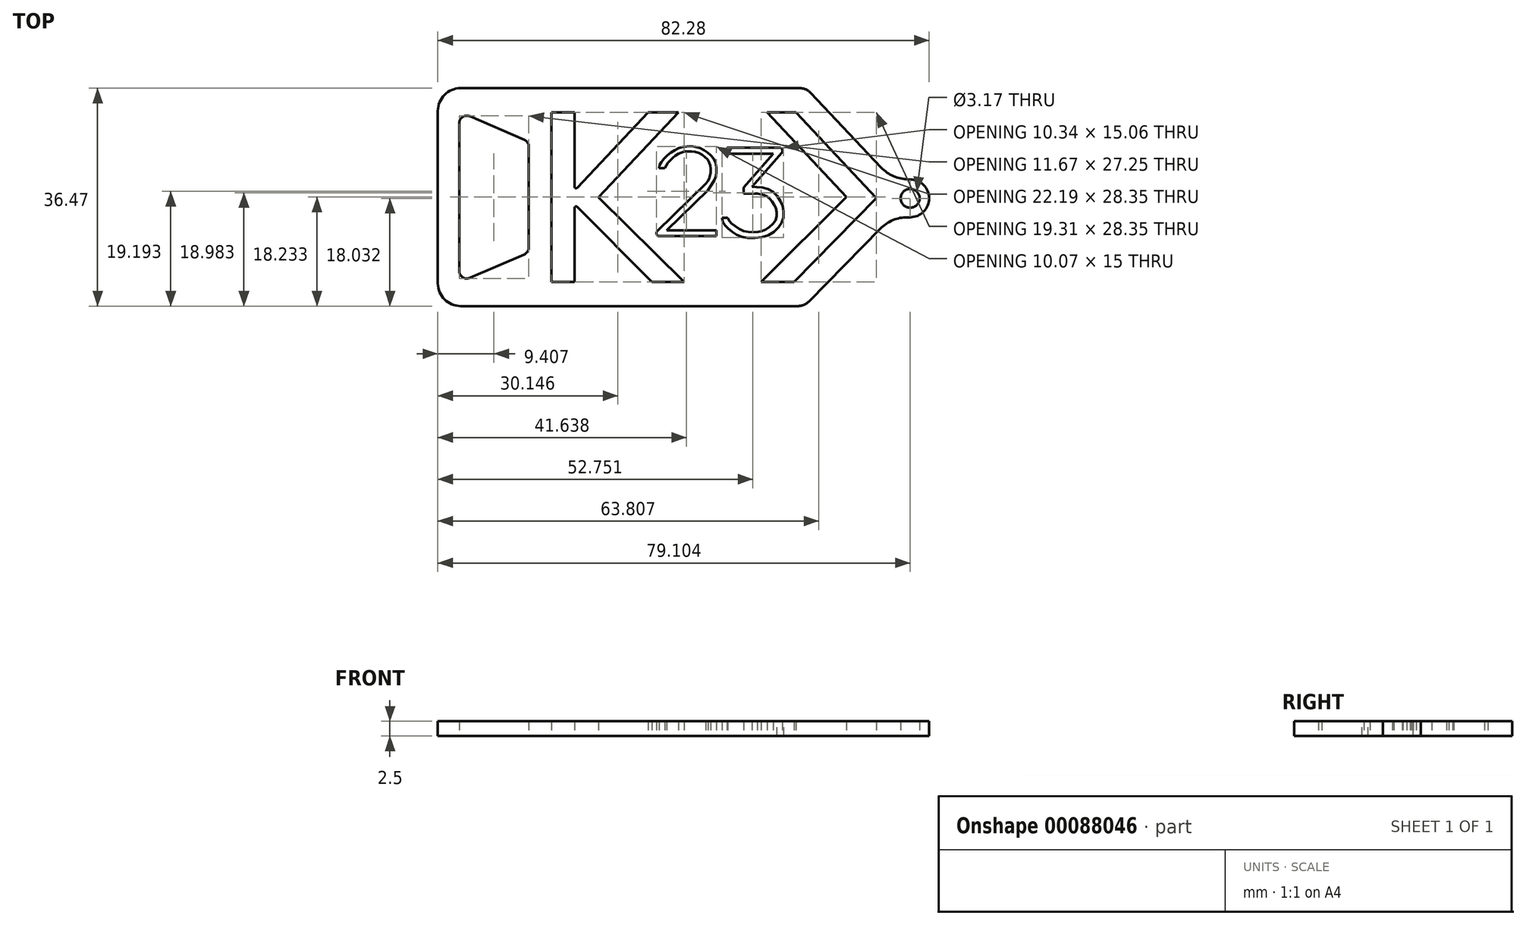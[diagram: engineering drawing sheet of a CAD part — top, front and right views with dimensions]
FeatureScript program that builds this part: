
annotation { "Feature Type Name" : "Feature", "Feature Type Description" : "" }
export const myFeature = defineFeature(function(context is Context, id is Id, definition is map)
    precondition{}
    {
        {
            var Q0;
            Q0=qCreatedBy(makeId("Top.planeOp"),FACE);
            var sketch = newSketch(context, id + "F0", { "sketchPlane" : qUnion([Q0])});
            skLineSegment(sketch, "E0", {"start": v(-56.05, -53.7) * mm, "end": v(-56.05, -52.7) * mm});
            skLineSegment(sketch, "E1", {"start": v(-56.05, -53.7) * mm, "end": v(-65.6, -53.7) * mm});
            skLineSegment(sketch, "E2", {"start": v(-65.96, -52.83) * mm, "end": v(-57.87, -44.95) * mm});
            skLineSegment(sketch, "E3", {"start": v(-56.05, -52.7) * mm, "end": v(-64.4, -52.7) * mm});
            skLineSegment(sketch, "E4", {"start": v(-64.4, -52.7) * mm, "end": v(-65.1, -52) * mm, "construction": true});
            skLineSegment(sketch, "E5", {"start": v(-64.4, -52.7) * mm, "end": v(-57.5, -45.98) * mm});
            skFitSpline(sketch, "E6", {"points": [v(-57.87, -44.95) * mm, v(-57.32, -44.18) * mm, v(-57.07, -43.34) * mm, v(-57.04, -42.12) * mm, v(-57.36, -41.17) * mm, v(-58.14, -40.3) * mm, v(-59.25, -39.7) * mm, v(-60.57, -39.5) * mm, v(-61.66, -39.6) * mm, v(-62.56, -40) * mm, v(-63.57, -40.77) * mm, v(-64.27, -41.53) * mm, v(-64.68, -42.35) * mm], "startDerivative": vector(10.41, 10.64) * mm, "endDerivative": vector(-4.73, -10.96) * mm});
            skLineSegment(sketch, "E7", {"start": v(-64.68, -42.35) * mm, "end": v(-65.68, -42.35) * mm});
            skFitSpline(sketch, "E8", {"points": [v(-65.68, -42.35) * mm, v(-65.54, -41.73) * mm, v(-65.05, -41) * mm, v(-64.16, -40.06) * mm, v(-63.3, -39.44) * mm, v(-62.23, -38.9) * mm, v(-61.22, -38.7) * mm, v(-60.27, -38.67) * mm, v(-59.04, -38.87) * mm, v(-57.9, -39.43) * mm, v(-57.12, -40.02) * mm, v(-56.37, -40.99) * mm, v(-56.08, -42.15) * mm, v(-56.1, -43.36) * mm, v(-56.37, -44.25) * mm, v(-57.5, -45.98) * mm], "startDerivative": vector(1.92, 12.36) * mm, "endDerivative": vector(-15.52, -18.51) * mm});
            skLineSegment(sketch, "E9", {"start": v(-54.29, -38.89) * mm, "end": v(-54.29, -39.89) * mm});
            skLineSegment(sketch, "E10", {"start": v(-54.29, -38.89) * mm, "end": v(-45.5, -38.89) * mm});
            skLineSegment(sketch, "E11", {"start": v(-45.12, -39.73) * mm, "end": v(-50.08, -45.46) * mm});
            skLineSegment(sketch, "E12", {"start": v(-54.29, -39.89) * mm, "end": v(-46.58, -39.89) * mm});
            skLineSegment(sketch, "E13", {"start": v(-46.58, -39.89) * mm, "end": v(-45.82, -40.54) * mm});
            skLineSegment(sketch, "E14", {"start": v(-46.58, -39.89) * mm, "end": v(-51.5, -45.58) * mm});
            skLineSegment(sketch, "E15", {"start": v(-51.5, -45.58) * mm, "end": v(-51.5, -46.58) * mm});
            skPoint(sketch, "E16.visualSharp", {"position": v(-44.39, -38.89) * mm});
            skArc(sketch, "E16.filletArc", {"start": v(-45.12, -39.73) * mm, "mid": v(-45.04, -39.18) * mm, "end": v(-45.5, -38.89) * mm});
            skPoint(sketch, "E17.visualSharp", {"position": v(-66.86, -53.7) * mm});
            skArc(sketch, "E17.filletArc", {"start": v(-65.96, -52.83) * mm, "mid": v(-66.08, -53.39) * mm, "end": v(-65.6, -53.7) * mm});
            skLineSegment(sketch, "E18", {"start": v(-51.5, -46.58) * mm, "end": v(-49.18, -46.58) * mm});
            skFitSpline(sketch, "E19", {"points": [v(-49.18, -46.58) * mm, v(-48.4, -46.73) * mm, v(-47.53, -47.1) * mm, v(-46.88, -47.72) * mm, v(-46.37, -48.48) * mm, v(-45.96, -49.59) * mm, v(-46.08, -50.86) * mm, v(-47.02, -52) * mm, v(-48.2, -52.78) * mm, v(-49.41, -53.02) * mm, v(-51.2, -52.93) * mm, v(-52.72, -52.2) * mm, v(-53.78, -51.3) * mm, v(-54.14, -50.65) * mm], "startDerivative": vector(12.2, -1.75) * mm, "endDerivative": vector(-3.87, 14.26) * mm});
            skLineSegment(sketch, "E20", {"start": v(-54.14, -50.65) * mm, "end": v(-55.14, -50.65) * mm});
            skFitSpline(sketch, "E21", {"points": [v(-55.14, -50.65) * mm, v(-54.93, -51.46) * mm, v(-54.52, -52.07) * mm, v(-53.73, -52.74) * mm, v(-52.54, -53.54) * mm, v(-51.15, -53.96) * mm, v(-48.91, -53.95) * mm, v(-46.89, -53.32) * mm, v(-45.54, -52.06) * mm, v(-44.89, -50.8) * mm, v(-44.85, -49.23) * mm, v(-45.25, -47.96) * mm, v(-46.29, -46.5) * mm, v(-47.53, -45.8) * mm, v(-49.08, -45.5) * mm, v(-50.08, -45.46) * mm], "startDerivative": vector(0.7, -15.69) * mm, "endDerivative": vector(-16.7, -0.1) * mm});
            skLineSegment(sketch, "E22", {"start": v(-42.77, -33) * mm, "end": v(-29.26, -47.3) * mm});
            skLineSegment(sketch, "E23", {"start": v(-29.26, -47.3) * mm, "end": v(-43.06, -61.34) * mm});
            skLineSegment(sketch, "E24", {"start": v(-43.06, -61.34) * mm, "end": v(-48.57, -61.34) * mm});
            skLineSegment(sketch, "E25", {"start": v(-83.67, -61.34) * mm, "end": v(-83.67, -33) * mm});
            skLineSegment(sketch, "E26", {"start": v(-79.82, -33) * mm, "end": v(-79.82, -45.42) * mm});
            skLineSegment(sketch, "E27", {"start": v(-66.89, -61.34) * mm, "end": v(-79.4, -48.8) * mm});
            skLineSegment(sketch, "E28", {"start": v(-61.48, -61.34) * mm, "end": v(-75.82, -47.2) * mm});
            skLineSegment(sketch, "E29", {"start": v(-75.82, -47.2) * mm, "end": v(-62.44, -33) * mm});
            skLineSegment(sketch, "E30", {"start": v(-79.39, -45.59) * mm, "end": v(-67.52, -33) * mm});
            skLineSegment(sketch, "E31", {"start": v(-48.57, -61.34) * mm, "end": v(-34.3, -47.17) * mm});
            skLineSegment(sketch, "E32", {"start": v(-34.3, -47.17) * mm, "end": v(-47.59, -33) * mm});
            skLineSegment(sketch, "E33.trimOffspring", {"start": v(-47.59, -33) * mm, "end": v(-42.77, -33) * mm});
            skLineSegment(sketch, "E34.trimOffspring", {"start": v(-67.52, -33) * mm, "end": v(-62.44, -33) * mm});
            skLineSegment(sketch, "E35.trimOffspring", {"start": v(-79.82, -48.98) * mm, "end": v(-79.82, -61.34) * mm});
            skLineSegment(sketch, "E36.trimOffspring", {"start": v(-79.82, -61.34) * mm, "end": v(-83.67, -61.34) * mm});
            skLineSegment(sketch, "E37.trimOffspring", {"start": v(-61.48, -61.34) * mm, "end": v(-66.89, -61.34) * mm});
            skLineSegment(sketch, "E38", {"start": v(-29.26, -61.34) * mm, "end": v(-29.26, -33) * mm, "construction": true});
            skLineSegment(sketch, "E39", {"start": v(-29.26, -33) * mm, "end": v(-83.67, -33) * mm, "construction": true});
            skLineSegment(sketch, "E40", {"start": v(-79.82, -33) * mm, "end": v(-83.67, -33) * mm});
            skLineSegment(sketch, "E41", {"start": v(-83.67, -33) * mm, "end": v(-83.67, -61.34) * mm, "construction": true});
            skLineSegment(sketch, "E42", {"start": v(-29.26, -61.34) * mm, "end": v(-83.67, -61.34) * mm, "construction": true});
            skLineSegment(sketch, "E43", {"start": v(-29.26, -47.17) * mm, "end": v(-26.78, -47.17) * mm, "construction": true});
            skLineSegment(sketch, "E44", {"start": v(-56.46, -28.75) * mm, "end": v(-56.46, -33) * mm, "construction": true});
            skLineSegment(sketch, "E45", {"start": v(-29.26, -47.17) * mm, "end": v(-83.67, -47.17) * mm, "construction": true});
            skLineSegment(sketch, "E46", {"start": v(-56.46, -33) * mm, "end": v(-56.46, -47.17) * mm, "construction": true});
            skPoint(sketch, "E47.visualSharp", {"position": v(-79.82, -46.06) * mm});
            skArc(sketch, "E47.filletArc", {"start": v(-79.82, -45.42) * mm, "mid": v(-79.66, -45.65) * mm, "end": v(-79.39, -45.59) * mm});
            skPoint(sketch, "E48.visualSharp", {"position": v(-79.82, -48.37) * mm});
            skArc(sketch, "E48.filletArc", {"start": v(-79.4, -48.8) * mm, "mid": v(-79.67, -48.75) * mm, "end": v(-79.82, -48.98) * mm});
            skLineSegment(sketch, "E49", {"start": v(-83.67, -33) * mm, "end": v(-83.67, -28.93) * mm});
            skLineSegment(sketch, "E50", {"start": v(-83.67, -28.93) * mm, "end": v(-41.02, -28.93) * mm});
            skLineSegment(sketch, "E51", {"start": v(-41.36, -65.4) * mm, "end": v(-87.48, -65.4) * mm});
            skLineSegment(sketch, "E52", {"start": v(-87.48, -55.6) * mm, "end": v(-87.48, -38.73) * mm});
            skLineSegment(sketch, "E53", {"start": v(-87.48, -28.93) * mm, "end": v(-83.67, -28.93) * mm});
            skLineSegment(sketch, "E54", {"start": v(-42.77, -33) * mm, "end": v(-39.81, -30.2) * mm, "construction": true});
            skLineSegment(sketch, "E55", {"start": v(-41.02, -28.93) * mm, "end": v(-28.5, -42.2) * mm});
            skLineSegment(sketch, "E56", {"start": v(-43.06, -61.34) * mm, "end": v(-40.16, -64.2) * mm, "construction": true});
            skLineSegment(sketch, "E57", {"start": v(-41.36, -65.4) * mm, "end": v(-28.6, -52.44) * mm});
            skArc(sketch, "E58", {"start": v(-23.62, -50.54) * mm, "mid": v(-20.44, -47.37) * mm, "end": v(-23.62, -44.2) * mm});
            skLineSegment(sketch, "E59", {"start": v(-23.62, -44.2) * mm, "end": v(-23.87, -44.2) * mm});
            skLineSegment(sketch, "E60", {"start": v(-23.62, -50.54) * mm, "end": v(-24.08, -50.54) * mm});
            skCircle(sketch, "E61", {"center": v(-23.62, -47.37) * mm, "radius": 1.59 * mm});
            skPoint(sketch, "E62.visualSharp", {"position": v(-26.61, -44.2) * mm});
            skArc(sketch, "E62.filletArc", {"start": v(-28.5, -42.2) * mm, "mid": v(-26.39, -43.67) * mm, "end": v(-23.87, -44.2) * mm});
            skPoint(sketch, "E63.visualSharp", {"position": v(-26.74, -50.54) * mm});
            skArc(sketch, "E63.filletArc", {"start": v(-24.08, -50.54) * mm, "mid": v(-26.53, -51.04) * mm, "end": v(-28.6, -52.44) * mm});
            skLineSegment(sketch, "E64", {"start": v(-88.25, -37.57) * mm, "end": v(-97.37, -33.64) * mm});
            skLineSegment(sketch, "E65", {"start": v(-88.25, -56.77) * mm, "end": v(-97.37, -60.7) * mm});
            skLineSegment(sketch, "E66", {"start": v(-87.48, -47.17) * mm, "end": v(-93.25, -47.17) * mm, "construction": true});
            skLineSegment(sketch, "E67", {"start": v(-99.15, -34.8) * mm, "end": v(-99.15, -59.53) * mm});
            skLineSegment(sketch, "E68", {"start": v(-87.48, -28.93) * mm, "end": v(-98.9, -28.93) * mm});
            skLineSegment(sketch, "E69", {"start": v(-102.72, -32.74) * mm, "end": v(-102.72, -61.6) * mm});
            skLineSegment(sketch, "E70", {"start": v(-98.9, -65.4) * mm, "end": v(-87.48, -65.4) * mm});
            skPoint(sketch, "E71.visualSharp", {"position": v(-102.72, -28.93) * mm});
            skArc(sketch, "E71.filletArc", {"start": v(-98.9, -28.93) * mm, "mid": v(-101.6, -30.04) * mm, "end": v(-102.72, -32.74) * mm});
            skPoint(sketch, "E72.visualSharp", {"position": v(-102.72, -65.4) * mm});
            skArc(sketch, "E72.filletArc", {"start": v(-102.72, -61.6) * mm, "mid": v(-101.6, -64.29) * mm, "end": v(-98.9, -65.4) * mm});
            skPoint(sketch, "E73.visualSharp", {"position": v(-99.15, -32.88) * mm});
            skArc(sketch, "E73.filletArc", {"start": v(-97.37, -33.64) * mm, "mid": v(-98.57, -33.75) * mm, "end": v(-99.15, -34.8) * mm});
            skPoint(sketch, "E74.visualSharp", {"position": v(-99.15, -61.45) * mm});
            skArc(sketch, "E74.filletArc", {"start": v(-99.15, -59.53) * mm, "mid": v(-98.57, -60.59) * mm, "end": v(-97.37, -60.7) * mm});
            skPoint(sketch, "E75.visualSharp", {"position": v(-87.48, -37.9) * mm});
            skArc(sketch, "E75.filletArc", {"start": v(-87.48, -38.73) * mm, "mid": v(-87.69, -38.03) * mm, "end": v(-88.25, -37.57) * mm});
            skPoint(sketch, "E76.visualSharp", {"position": v(-87.48, -56.44) * mm});
            skArc(sketch, "E76.filletArc", {"start": v(-88.25, -56.77) * mm, "mid": v(-87.69, -56.3) * mm, "end": v(-87.48, -55.6) * mm});
            skSolve(sketch);
        }
        {
            var Q0;
            Q0=makeQuery(id+"F0.imprint","IMPRINT",FACE,{"disambiguationData":[TD([[makeQuery(id+"F0.imprint","IMPRINT",EDGE,{"derivedFrom":sQuery(id+"F0.wireOp",EDGE,"E0")}),-1.0]])]});
            extrude(context, id + "F1", {"entities" : qUnion([Q0]), "depth" : 2.5 * mm});
        }
        {
            var Q0;
            Q0=makeQuery(id+"F1.opExtrude","SWEPT_EDGE",EDGE,{"disambiguationData":[OSD([sQuery(id+"F0.wireOp",EDGE,"E50"),sQuery(id+"F0.wireOp",EDGE,"E55")])]});
            var Q1;
            Q1=makeQuery(id+"F1.opExtrude","SWEPT_EDGE",EDGE,{"disambiguationData":[OSD([sQuery(id+"F0.wireOp",EDGE,"E51"),sQuery(id+"F0.wireOp",EDGE,"E57")])]});
            fillet(context, id + "F2", {"entities" : qUnion([Q0, Q1]), "radius" : 2.54 * mm, "tangentPropagation" : true, "allowEdgeOverflow" : false});
        }
    });
